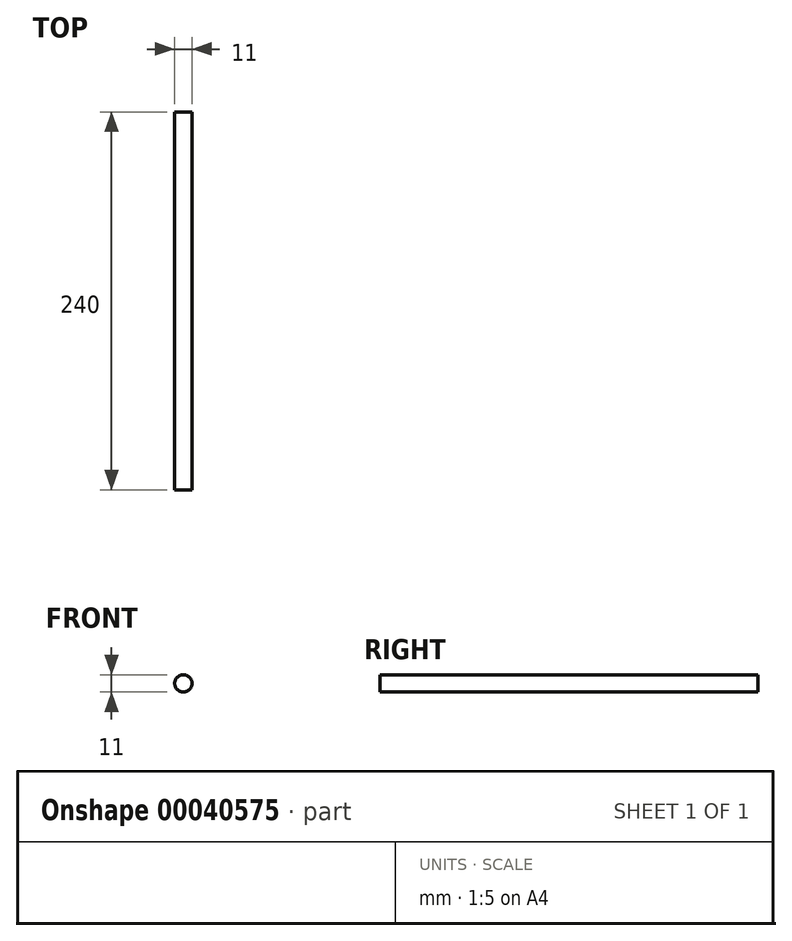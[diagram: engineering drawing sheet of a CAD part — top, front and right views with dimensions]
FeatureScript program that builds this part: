
annotation { "Feature Type Name" : "Feature", "Feature Type Description" : "" }
export const myFeature = defineFeature(function(context is Context, id is Id, definition is map)
    precondition{}
    {
        {
            var Q0;
            Q0=qCreatedBy(makeId("Front.planeOp"),FACE);
            var sketch = newSketch(context, id + "F0", { "sketchPlane" : qUnion([Q0])});
            skCircle(sketch, "E0", {"center": v(0, 0) * mm, "radius": 5.5 * mm});
            skSolve(sketch);
        }
        {
            var Q0;
            Q0 = qSketchRegion(id + "F0", true);
            extrude(context, id + "F1", {"entities" : qUnion([Q0]), "depth" : 240 * mm});
        }
    });
